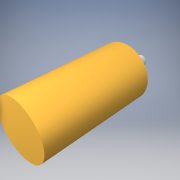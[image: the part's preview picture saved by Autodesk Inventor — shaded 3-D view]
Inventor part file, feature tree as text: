
AUTODESK INVENTOR PART (.ipt)
format: ipt  version: 2016 (Build 200138000, 138)  size: 110,592 bytes
history: native  units: mm
features: extrude x2, sketch x2, other x1
ambient origin geometry x8: Origin, YZ Plane, XZ Plane, XY Plane, X Axis, Y Axis, Z Axis, Center Point
bodies: Body1 (feature_tree)
feature tree (5):
  other  "ソリッド1"
  extrude  "押し出し1"  Depth=10.0mm
  extrude  "押し出し2"  Depth=20.0mm TaperAngle=0.0deg
  sketch  "スケッチ1"
  sketch  "スケッチ2"
